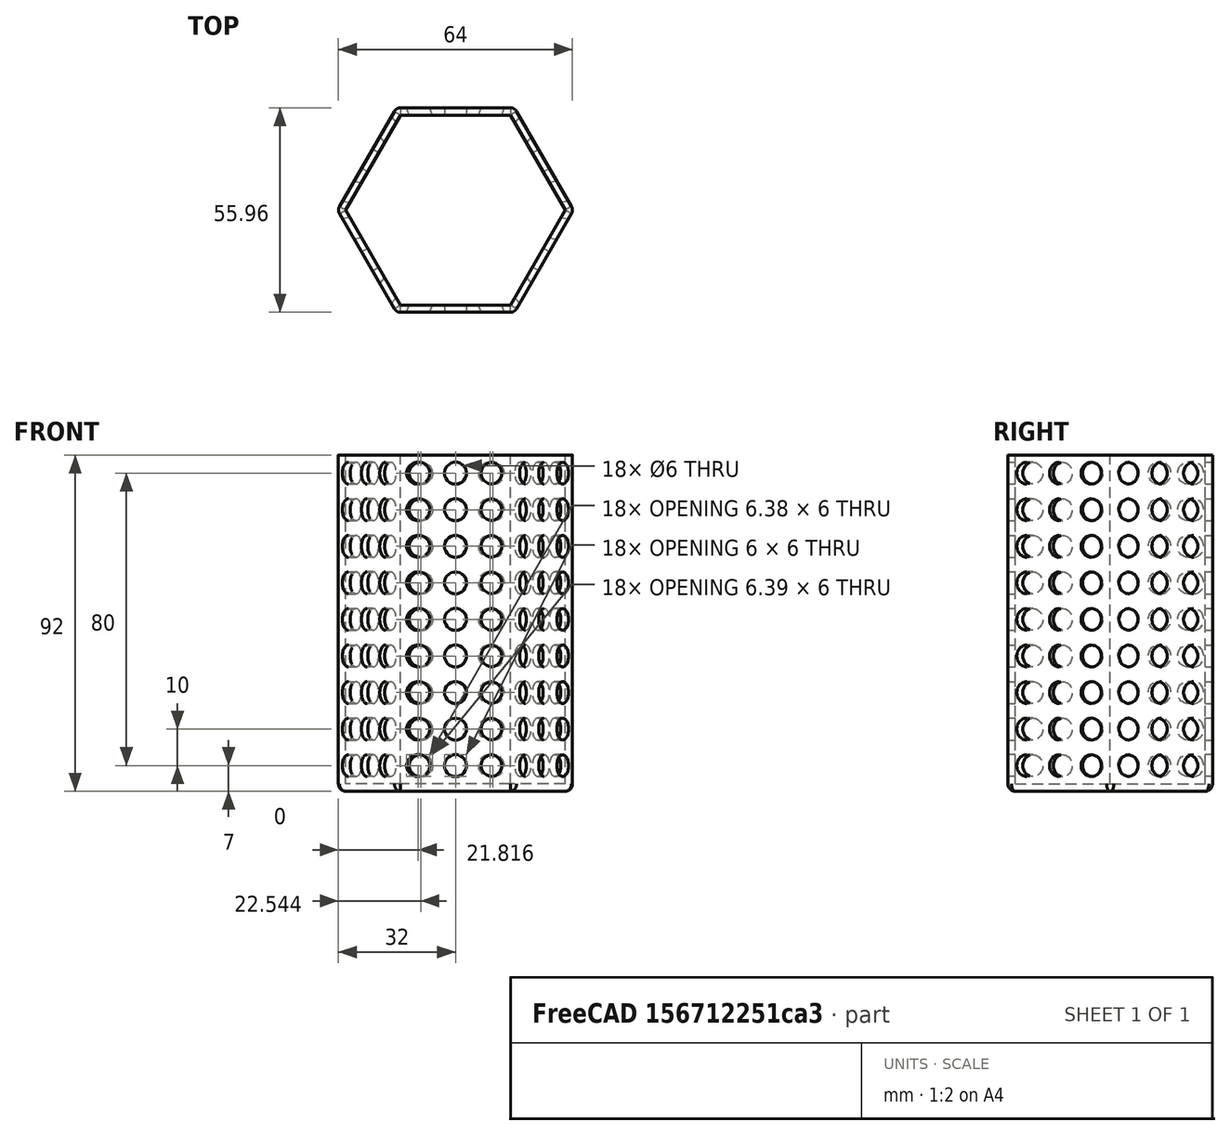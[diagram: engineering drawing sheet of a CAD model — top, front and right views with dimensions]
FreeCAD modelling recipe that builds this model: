
FCSTD DOCUMENT  (FreeCAD 0.16R6707 (Git))
Label: cubilete_curso_frrecad
License: All rights reserved
LicenseURL: http://en.wikipedia.org/wiki/All_rights_reserved
objects: Part::FeaturePython×2, Part::Prism×1, Part::Thickness×1, Part::Cylinder×1, Part::Cut×1
note: 6 computed .brp shape members not serialized (recipe doc carries the construction recipe); baked Part::Feature solids carry a one-line shape summary decoded from their .brp

FEATURE [Part::Prism] Prism  label="Prisma"
  Circumradius = 30
  Height = 90
  Polygon = 6
FEATURE [Part::Thickness] Thickness  label="cubilete solido"
  Faces = -> Prism [Face8]
  Intersection = false
  Join = 0
  Mode = 0
  SelfIntersection = false
  Value = 2
FEATURE [Part::Cylinder] Cylinder  label="Cilindro"
  Angle = 360
  Height = 80
  Placement = pos=(-34.641,-20,5) rot=(-0.250563,0.935113,0.250563;1.63783rad)
  Radius = 3
FEATURE [Part::FeaturePython] Array  # Draft array (typed FeaturePython)
  Angle = 360
  ArrayType = 0
  Axis = (0,0,1)
  Base = -> Cylinder
  Center = (0,0,0)
  IntervalX = (1,0,0)
  IntervalY = (0,1,0)
  IntervalZ = (0,0,10)
  NumberPolar = 1
  NumberX = 1
  NumberY = 1
  NumberZ = 9
FEATURE [Part::FeaturePython] Array001  label="Taladros"  # Draft array (typed FeaturePython)
  Angle = 360
  ArrayType = 1
  Axis = (0,0,1)
  Base = -> Array
  Center = (0,0,0)
  IntervalX = (1,0,0)
  IntervalY = (0,1,0)
  IntervalZ = (0,0,1)
  NumberPolar = 9
  NumberX = 1
  NumberY = 1
  NumberZ = 1
FEATURE [Part::Cut] Cut  label="cubilete_bolis"
  Base = -> Thickness
  Tool = -> Array001
